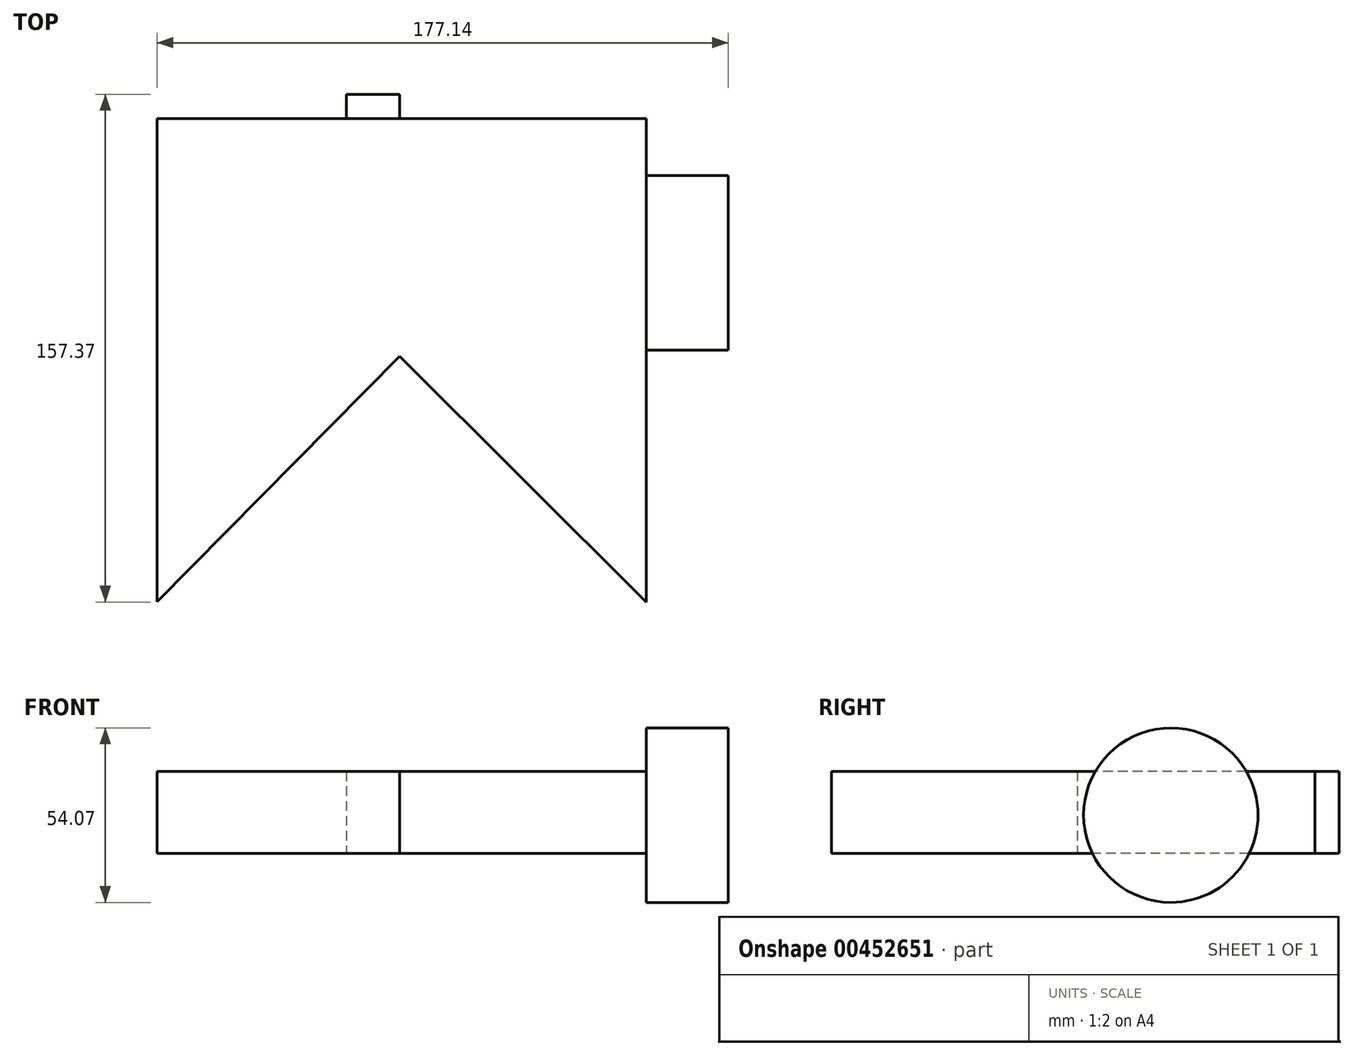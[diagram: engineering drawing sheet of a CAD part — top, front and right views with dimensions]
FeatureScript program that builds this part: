
annotation { "Feature Type Name" : "Feature", "Feature Type Description" : "" }
export const myFeature = defineFeature(function(context is Context, id is Id, definition is map)
    precondition{}
    {
        {
            var Q0;
            Q0=qCreatedBy(makeId("Top.planeOp"),FACE);
            var sketch = newSketch(context, id + "F0", { "sketchPlane" : qUnion([Q0])});
            skLineSegment(sketch, "E0", {"start": v(0, 0) * mm, "end": v(-75.22, -76.08) * mm});
            skLineSegment(sketch, "E1", {"start": v(-75.22, -76.08) * mm, "end": v(-75.22, 73.63) * mm});
            skLineSegment(sketch, "E2", {"start": v(-75.22, 73.63) * mm, "end": v(76.52, 73.63) * mm});
            skLineSegment(sketch, "E3", {"start": v(76.52, 73.63) * mm, "end": v(76.52, -76.22) * mm});
            skLineSegment(sketch, "E4", {"start": v(76.52, -76.22) * mm, "end": v(0, 0) * mm});
            skSolve(sketch);
        }
        {
            var Q0;
            Q0=qCreatedBy(makeId("Front.planeOp"),FACE);
            var sketch = newSketch(context, id + "F1", { "sketchPlane" : qUnion([Q0])});
            skLineSegment(sketch, "E5", {"start": v(0, 0) * mm, "end": v(0, 83.98) * mm});
            skSolve(sketch);
        }
        {
            var Q0;
            Q0=makeQuery(id+"F0.imprint","IMPRINT",FACE,{"disambiguationData":[TD([[makeQuery(id+"F0.imprint","IMPRINT",EDGE,{"derivedFrom":sQuery(id+"F0.wireOp",EDGE,"E0")}),-1.0]])]});
            var sketch = newSketch(context, id + "F2", { "sketchPlane" : qUnion([Q0])});
            skLineSegment(sketch, "E6.bottom", {"start": v(-16.51, 81.15) * mm, "end": v(0, 81.15) * mm});
            skLineSegment(sketch, "E6.top", {"start": v(-16.51, 0) * mm, "end": v(0, 0) * mm});
            skLineSegment(sketch, "E6.left", {"start": v(-16.51, 81.15) * mm, "end": v(-16.51, 0) * mm});
            skLineSegment(sketch, "E6.right", {"start": v(0, 81.15) * mm, "end": v(0, 0) * mm});
            skSolve(sketch);
        }
        {
            var Q0;
            Q0=makeQuery(id+"F0.imprint","IMPRINT",FACE,{"disambiguationData":[TD([[makeQuery(id+"F0.imprint","IMPRINT",EDGE,{"derivedFrom":sQuery(id+"F0.wireOp",EDGE,"E0")}),-1.0]])]});
            var Q1;
            {var subQ0=sQuery(id+"F2.wireOp",EDGE,"E6.bottom");Q1=makeQuery(id+"F2.imprint","IMPRINT",FACE,{"disambiguationData":[TD([[makeQuery(id+"F2.imprint","IMPRINT",EDGE,{"derivedFrom":subQ0}),-1.0]])]});}
            var Q2;
            Q2=sQuery(id+"F1.wireOp",EDGE,"E5");
            var Q3;
            Q3=sQuery(id+"F0.wireOp",EDGE,"E2");
            var Q4;
            Q4=sQuery(id+"F2.wireOp",EDGE,"E6.bottom");
            var Q5;
            Q5=sQuery(id+"F2.wireOp",EDGE,"E6.right");
            var Q6;
            Q6=sQuery(id+"F2.wireOp",EDGE,"E6.left");
            extrude(context, id + "F3", {"entities" : qUnion([Q0, Q1]), "surfaceEntities" : qUnion([Q2, Q3, Q4, Q5, Q6]), "depth" : 25.4 * mm});
        }
        {
            var Q0;
            Q0=makeQuery(id+"F3.opExtrude","SWEPT_FACE",FACE,{"disambiguationData":[OSD([sQuery(id+"F0.wireOp",EDGE,"E3")])]});
            var sketch = newSketch(context, id + "F4", { "sketchPlane" : qUnion([Q0])});
            skCircle(sketch, "E7", {"center": v(28.94, 11.86) * mm, "radius": 27.03 * mm});
            skSolve(sketch);
        }
        {
            var Q0;
            Q0 = qSketchRegion(id + "F4", true);
            extrude(context, id + "F5", {"entities" : qUnion([Q0]), "operationType" : NewBodyOperationType.ADD, "depth" : 25.4 * mm});
        }
    });
